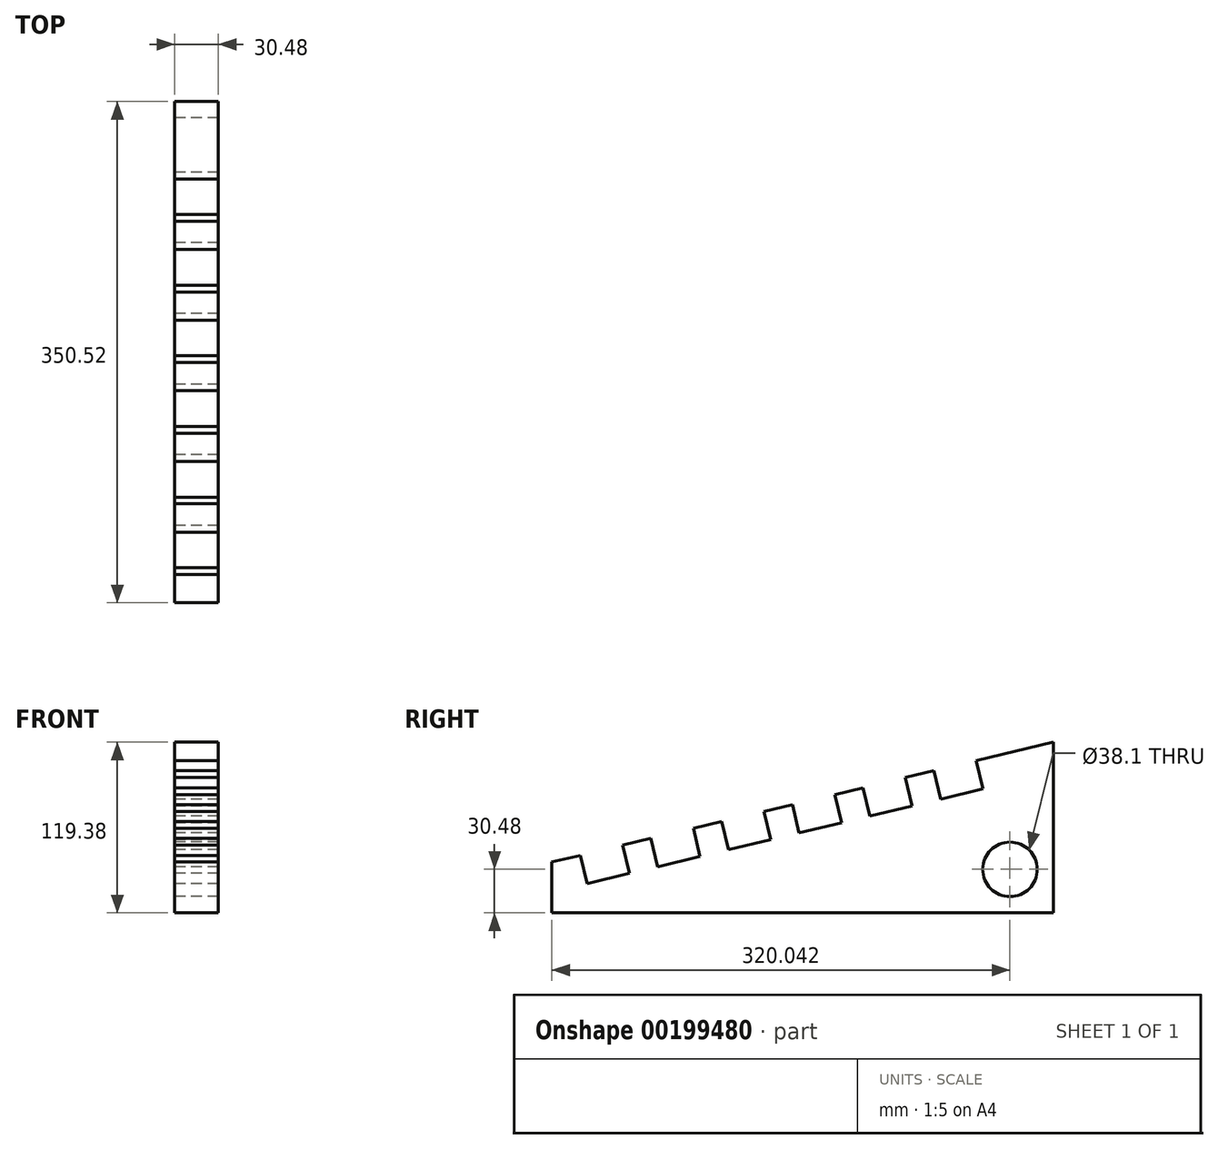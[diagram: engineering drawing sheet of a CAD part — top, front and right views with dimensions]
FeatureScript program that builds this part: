
annotation { "Feature Type Name" : "Feature", "Feature Type Description" : "" }
export const myFeature = defineFeature(function(context is Context, id is Id, definition is map)
    precondition{}
    {
        {
            var Q0;
            Q0=qCreatedBy(makeId("Right.planeOp"),FACE);
            var sketch = newSketch(context, id + "F0", { "sketchPlane" : qUnion([Q0])});
            skLineSegment(sketch, "E0", {"start": v(-163.62, 0) * mm, "end": v(-163.62, 35.56) * mm});
            skLineSegment(sketch, "E1", {"start": v(-163.62, 0) * mm, "end": v(186.9, 0) * mm});
            skLineSegment(sketch, "E2", {"start": v(186.9, 0) * mm, "end": v(186.9, 119.38) * mm});
            skLineSegment(sketch, "E3", {"start": v(-163.62, 35.56) * mm, "end": v(-143.86, 40.29) * mm});
            skLineSegment(sketch, "E4", {"start": v(-143.86, 40.29) * mm, "end": v(-139.13, 20.52) * mm});
            skLineSegment(sketch, "E5", {"start": v(-139.13, 20.52) * mm, "end": v(-109.49, 27.61) * mm});
            skLineSegment(sketch, "E6", {"start": v(-109.49, 27.61) * mm, "end": v(-114.21, 47.37) * mm});
            skLineSegment(sketch, "E7", {"start": v(-114.21, 47.37) * mm, "end": v(-94.45, 52.1) * mm});
            skLineSegment(sketch, "E8", {"start": v(-94.45, 52.1) * mm, "end": v(-89.72, 32.34) * mm});
            skLineSegment(sketch, "E9", {"start": v(-89.72, 32.34) * mm, "end": v(-60.08, 39.43) * mm});
            skLineSegment(sketch, "E10", {"start": v(-60.08, 39.43) * mm, "end": v(-64.8, 59.19) * mm});
            skLineSegment(sketch, "E11", {"start": v(-64.8, 59.19) * mm, "end": v(-45.04, 63.92) * mm});
            skLineSegment(sketch, "E12", {"start": v(-45.04, 63.92) * mm, "end": v(-40.32, 44.15) * mm});
            skLineSegment(sketch, "E13", {"start": v(-40.32, 44.15) * mm, "end": v(-10.67, 51.24) * mm});
            skLineSegment(sketch, "E14", {"start": v(-10.67, 51.24) * mm, "end": v(-15.4, 71) * mm});
            skLineSegment(sketch, "E15", {"start": v(-15.4, 71) * mm, "end": v(4.37, 75.73) * mm});
            skLineSegment(sketch, "E16", {"start": v(4.37, 75.73) * mm, "end": v(9.1, 55.97) * mm});
            skLineSegment(sketch, "E17", {"start": v(9.1, 55.97) * mm, "end": v(38.74, 63.06) * mm});
            skLineSegment(sketch, "E18", {"start": v(38.74, 63.06) * mm, "end": v(34, 82.82) * mm});
            skLineSegment(sketch, "E19", {"start": v(34, 82.82) * mm, "end": v(53.77, 87.54) * mm});
            skLineSegment(sketch, "E20", {"start": v(53.77, 87.54) * mm, "end": v(58.5, 67.78) * mm});
            skLineSegment(sketch, "E21", {"start": v(58.5, 67.78) * mm, "end": v(88.14, 74.87) * mm});
            skLineSegment(sketch, "E22", {"start": v(88.14, 74.87) * mm, "end": v(83.42, 94.63) * mm});
            skLineSegment(sketch, "E23", {"start": v(83.42, 94.63) * mm, "end": v(103.18, 99.36) * mm});
            skLineSegment(sketch, "E24", {"start": v(103.18, 99.36) * mm, "end": v(107.9, 79.6) * mm});
            skLineSegment(sketch, "E25", {"start": v(107.9, 79.6) * mm, "end": v(137.55, 86.69) * mm});
            skLineSegment(sketch, "E26", {"start": v(137.55, 86.69) * mm, "end": v(132.82, 106.45) * mm});
            skLineSegment(sketch, "E27", {"start": v(132.82, 106.45) * mm, "end": v(186.9, 119.38) * mm});
            skSolve(sketch);
        }
        {
            var Q0;
            Q0 = qSketchRegion(id + "F0", true);
            extrude(context, id + "F1", {"entities" : qUnion([Q0]), "depth" : 30.48 * mm});
        }
        {
            var Q0;
            Q0=makeQuery(id+"F1.opExtrude","CAP_FACE",FACE,{"disambiguationData":[OSD([sQuery(id+"F0.wireOp",EDGE,"E0"),sQuery(id+"F0.wireOp",EDGE,"E1"),sQuery(id+"F0.wireOp",EDGE,"E2"),sQuery(id+"F0.wireOp",EDGE,"E3"),sQuery(id+"F0.wireOp",EDGE,"E4"),sQuery(id+"F0.wireOp",EDGE,"E5"),sQuery(id+"F0.wireOp",EDGE,"E6"),sQuery(id+"F0.wireOp",EDGE,"E7"),sQuery(id+"F0.wireOp",EDGE,"E8"),sQuery(id+"F0.wireOp",EDGE,"E9"),sQuery(id+"F0.wireOp",EDGE,"E10"),sQuery(id+"F0.wireOp",EDGE,"E11"),sQuery(id+"F0.wireOp",EDGE,"E12"),sQuery(id+"F0.wireOp",EDGE,"E13"),sQuery(id+"F0.wireOp",EDGE,"E14"),sQuery(id+"F0.wireOp",EDGE,"E15"),sQuery(id+"F0.wireOp",EDGE,"E16"),sQuery(id+"F0.wireOp",EDGE,"E17"),sQuery(id+"F0.wireOp",EDGE,"E18"),sQuery(id+"F0.wireOp",EDGE,"E19"),sQuery(id+"F0.wireOp",EDGE,"E20"),sQuery(id+"F0.wireOp",EDGE,"E21"),sQuery(id+"F0.wireOp",EDGE,"E22"),sQuery(id+"F0.wireOp",EDGE,"E23"),sQuery(id+"F0.wireOp",EDGE,"E24"),sQuery(id+"F0.wireOp",EDGE,"E25"),sQuery(id+"F0.wireOp",EDGE,"E26"),sQuery(id+"F0.wireOp",EDGE,"E27")])],"isStart":true});
            var sketch = newSketch(context, id + "F2", { "sketchPlane" : qUnion([Q0])});
            skCircle(sketch, "E28", {"center": v(-156.42, 30.48) * mm, "radius": 19.05 * mm});
            skPoint(sketch, "E28.first.point", {"position": v(-169.66, 16.78) * mm});
            skPoint(sketch, "E28.second.point", {"position": v(-159.44, 11.67) * mm});
            skPoint(sketch, "E28.third.point", {"position": v(-140.56, 19.93) * mm});
            skSolve(sketch);
        }
        {
            var Q0;
            Q0 = qSketchRegion(id + "F2", true);
            extrude(context, id + "F3", {"entities" : qUnion([Q0]), "operationType" : NewBodyOperationType.REMOVE, "endBound" : BoundingType.UP_TO_NEXT, "oppositeDirection" : true, "depth" : 25.4 * mm});
        }
    });
